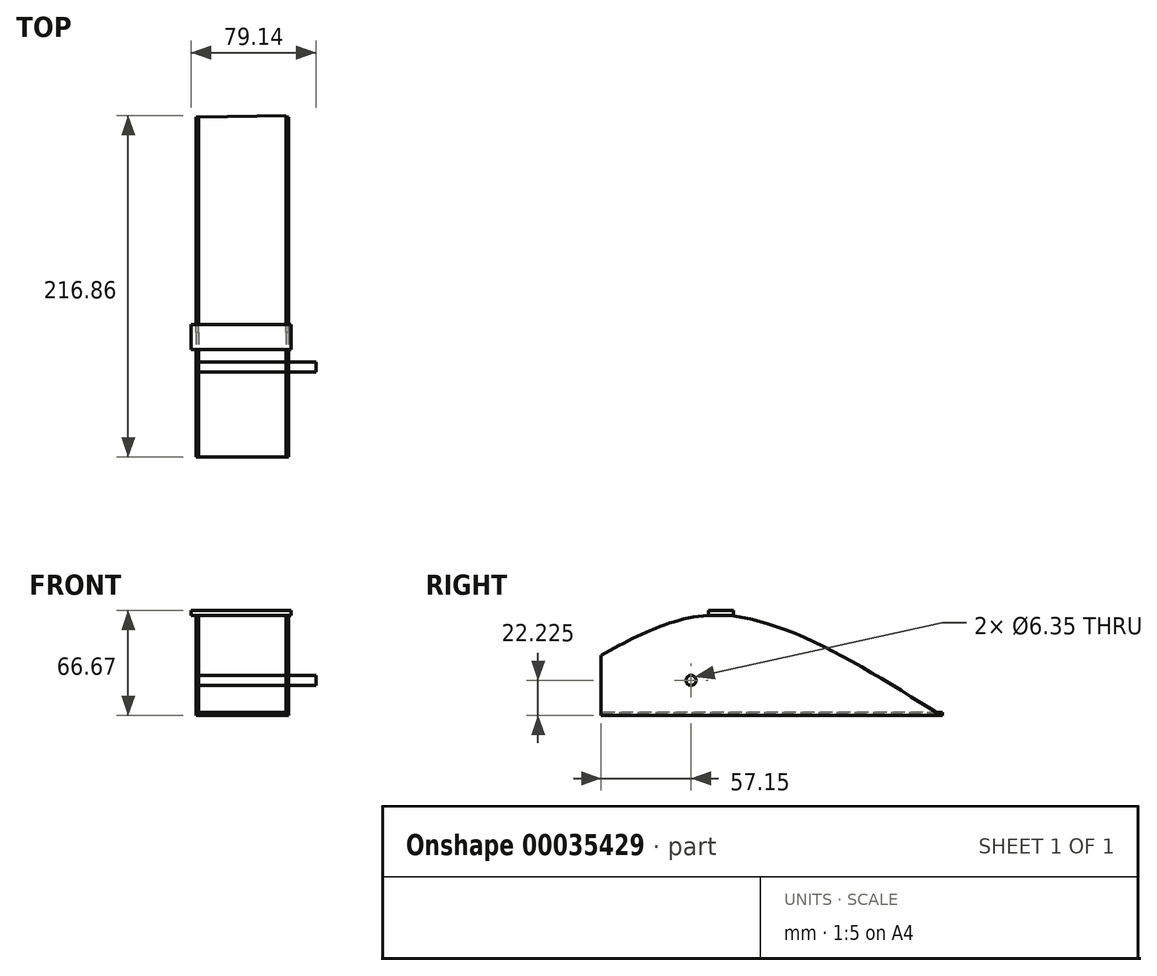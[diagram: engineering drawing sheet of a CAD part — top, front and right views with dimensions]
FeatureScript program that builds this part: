
annotation { "Feature Type Name" : "Feature", "Feature Type Description" : "" }
export const myFeature = defineFeature(function(context is Context, id is Id, definition is map)
    precondition{}
    {
        {
            var Q0;
            Q0=qCreatedBy(makeId("Right.planeOp"),FACE);
            var sketch = newSketch(context, id + "F0", { "sketchPlane" : qUnion([Q0])});
            skLineSegment(sketch, "E0.rect.bottom", {"start": v(-28.97, 31.75) * mm, "end": v(-39.73, 31.75) * mm});
            skLineSegment(sketch, "E0.rect.top", {"start": v(107.95, -31.75) * mm, "end": v(-107.95, -31.75) * mm});
            skLineSegment(sketch, "E0.rect.right", {"start": v(-107.95, 6.42) * mm, "end": v(-107.95, -31.75) * mm});
            skPoint(sketch, "E0.rect.middle", {"position": v(0, 0) * mm});
            skFitSpline(sketch, "E1", {"points": [v(-107.95, 6.42) * mm, v(-28.97, 31.75) * mm, v(107.95, -31.75) * mm], "startDerivative": vector(174.27, 95.7) * mm, "endDerivative": vector(253.6, -159.4) * mm});
            skPoint(sketch, "E2.orphan", {"position": v(-107.95, 31.75) * mm});
            skPoint(sketch, "E0.rect.left.start.orphan", {"position": v(107.95, 31.75) * mm});
            skSolve(sketch);
        }
        {
            var Q0;
            {var subQ2=sQuery(id+"F0.wireOp",EDGE,"E0.rect.bottom");Q0=makeQuery(id+"F0.imprint","IMPRINT",FACE,{"disambiguationData":[TD([[makeQuery(id+"F0.imprint","IMPRINT",EDGE,{"derivedFrom":subQ2}),1.0]])]});}
            extrude(context, id + "F1", {"entities" : qUnion([Q0]), "depth" : 1.75 * mm});
        }
        {
            var Q0;
            Q0=makeQuery(id+"F1.opExtrude","SWEPT_BODY",BODY,{"disambiguationData":[OSD([sQuery(id+"F0.wireOp",EDGE,"E0.rect.bottom"),sQuery(id+"F0.wireOp",EDGE,"E0.rect.top"),sQuery(id+"F0.wireOp",EDGE,"E0.rect.right"),sQuery(id+"F0.wireOp",EDGE,"E1")])]});
            transform(context, id + "F2", {"entities" : qUnion([Q0]), "transformType" : TransformType.TRANSLATION_3D, "dx" : -57.15 * mm, "dy" : 0 * mm, "dz" : 0 * mm, "makeCopy" : true});
        }
        {
            var Q0;
            Q0=makeQuery(id+"F2.opPattern","COPY",FACE,{"derivedFrom":makeQuery(id+"F1.opExtrude","SWEPT_FACE",FACE,{"disambiguationData":[OSD([sQuery(id+"F0.wireOp",EDGE,"E0.rect.top")])]}),"instanceName":"1"});
            var sketch = newSketch(context, id + "F3", { "sketchPlane" : qUnion([Q0])});
            skLineSegment(sketch, "E3", {"start": v(-55.4, 107.95) * mm, "end": v(0, 107.95) * mm});
            skLineSegment(sketch, "E4", {"start": v(0, 107.95) * mm, "end": v(0, -108.91) * mm});
            skLineSegment(sketch, "E5", {"start": v(0, -108.91) * mm, "end": v(-55.4, -107.95) * mm});
            skLineSegment(sketch, "E6", {"start": v(-55.4, -107.95) * mm, "end": v(-55.4, 107.95) * mm});
            skSolve(sketch);
        }
        {
            var Q0;
            Q0 = qSketchRegion(id + "F3", true);
            extrude(context, id + "F4", {"entities" : qUnion([Q0]), "oppositeDirection" : true, "depth" : 1.9 * mm});
        }
        {
            var Q0;
            Q0=makeQuery(id+"F2.opPattern","COPY",FACE,{"derivedFrom":makeQuery(id+"F1.opExtrude","SWEPT_FACE",FACE,{"disambiguationData":[OSD([sQuery(id+"F0.wireOp",EDGE,"E0.rect.bottom")])]}),"instanceName":"1"});
            var sketch = newSketch(context, id + "F5", { "sketchPlane" : qUnion([Q0])});
            skLineSegment(sketch, "E7.bottom", {"start": v(-60.1, -39.73) * mm, "end": v(3.4, -39.73) * mm});
            skLineSegment(sketch, "E7.top", {"start": v(-60.1, -23.86) * mm, "end": v(3.4, -23.86) * mm});
            skLineSegment(sketch, "E7.left", {"start": v(-60.1, -39.73) * mm, "end": v(-60.1, -23.86) * mm});
            skLineSegment(sketch, "E7.right", {"start": v(3.4, -39.73) * mm, "end": v(3.4, -23.86) * mm});
            skSolve(sketch);
        }
        {
            var Q0;
            Q0=makeQuery(id+"F2.opPattern","COPY",FACE,{"derivedFrom":makeQuery(id+"F1.opExtrude","CAP_FACE",FACE,{"disambiguationData":[OSD([sQuery(id+"F0.wireOp",EDGE,"E0.rect.bottom"),sQuery(id+"F0.wireOp",EDGE,"E0.rect.top"),sQuery(id+"F0.wireOp",EDGE,"E0.rect.right"),sQuery(id+"F0.wireOp",EDGE,"E1")])],"isStart":true}),"instanceName":"1"});
            var sketch = newSketch(context, id + "F6", { "sketchPlane" : qUnion([Q0])});
            skCircle(sketch, "E8", {"center": v(50.8, -9.52) * mm, "radius": 3.18 * mm});
            skSolve(sketch);
        }
        {
            var Q0;
            Q0=makeQuery(id+"F6.imprint","IMPRINT",FACE,{"disambiguationData":[TD([[makeQuery(id+"F6.imprint","IMPRINT",EDGE,{"derivedFrom":sQuery(id+"F6.wireOp",EDGE,"E8")}),1.0]])]});
            extrude(context, id + "F7", {"entities" : qUnion([Q0]), "operationType" : NewBodyOperationType.REMOVE, "endBound" : BoundingType.THROUGH_ALL, "oppositeDirection" : true, "depth" : 25.4 * mm});
        }
        {
            var Q0;
            Q0 = qSketchRegion(id + "F5", true);
            extrude(context, id + "F8", {"entities" : qUnion([Q0]), "depth" : 3.17 * mm});
        }
        {
            var Q0;
            Q0=makeQuery(id+"F1.opExtrude","CAP_FACE",FACE,{"disambiguationData":[OSD([sQuery(id+"F0.wireOp",EDGE,"E0.rect.bottom"),sQuery(id+"F0.wireOp",EDGE,"E0.rect.top"),sQuery(id+"F0.wireOp",EDGE,"E0.rect.right"),sQuery(id+"F0.wireOp",EDGE,"E1")])],"isStart":false});
            var sketch = newSketch(context, id + "F9", { "sketchPlane" : qUnion([Q0])});
            skCircle(sketch, "E9", {"center": v(-50.8, -9.52) * mm, "radius": 3.18 * mm});
            skSolve(sketch);
        }
        {
            var Q0;
            Q0=makeQuery(id+"F9.imprint","IMPRINT",FACE,{"disambiguationData":[TD([[makeQuery(id+"F9.imprint","IMPRINT",EDGE,{"derivedFrom":sQuery(id+"F9.wireOp",EDGE,"E9")}),1.0]])]});
            extrude(context, id + "F10", {"entities" : qUnion([Q0]), "operationType" : NewBodyOperationType.REMOVE, "endBound" : BoundingType.THROUGH_ALL, "oppositeDirection" : true, "depth" : 25.4 * mm});
        }
        {
            var Q0;
            Q0=makeQuery(id+"F6.imprint","IMPRINT",FACE,{"disambiguationData":[TD([[makeQuery(id+"F6.imprint","IMPRINT",EDGE,{"derivedFrom":sQuery(id+"F6.wireOp",EDGE,"E8")}),1.0]])]});
            var Q1;
            Q1=sQuery(id+"F6.wireOp",EDGE,"E8");
            extrude(context, id + "F11", {"entities" : qUnion([Q0]), "surfaceEntities" : qUnion([Q1]), "oppositeDirection" : true, "depth" : 76.2 * mm});
        }
    });
